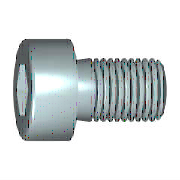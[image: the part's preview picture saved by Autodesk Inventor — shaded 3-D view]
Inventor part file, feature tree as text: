
AUTODESK INVENTOR PART (.ipt)
format: ipt  version: 2022 (Build 260153000, 153)  size: 190,976 bytes
history: native  units: mm (DEFAULTED — no unit token found)
features: sketch x2, other x1, extrude x1, plane x1, fillet x1
ambient origin geometry x7: Origin, YZ Plane, XY Plane, X Axis, Y Axis, Z Axis, Center Point
bodies: Solid1 (feature_tree)
feature tree (6):
  other  "Базовый элемент"
  extrude  "Паз"  Depth=14.0mm
  plane  "Work Plane1"
  fillet  "Fillet2"  Radius=0.429515mm
  sketch  "Эскиз1"
  sketch  "Эскиз2"
